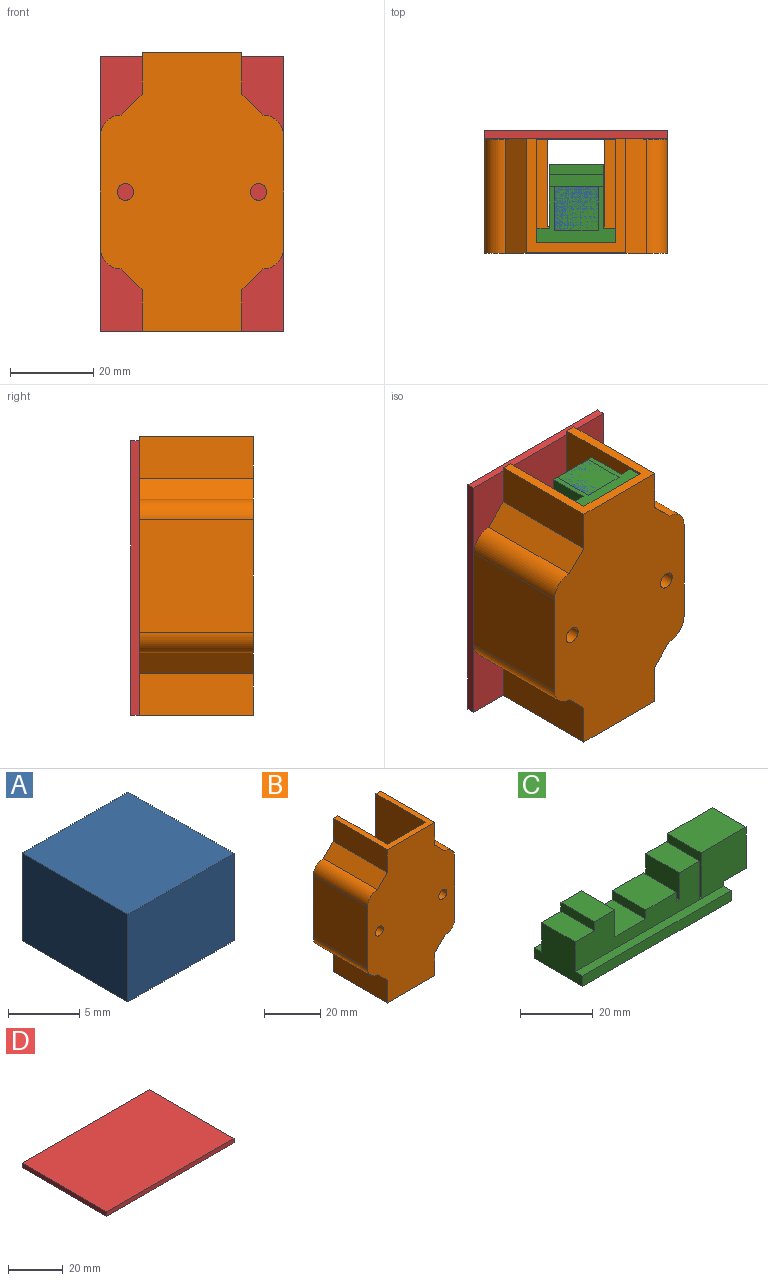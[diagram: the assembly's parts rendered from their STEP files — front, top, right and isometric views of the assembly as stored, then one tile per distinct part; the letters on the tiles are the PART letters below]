
ASSEMBLY  parts=4 mates=6
PART A: 10 faces, bbox 10.5x10.5x7.5 mm
  f0: plane 3.5x3.5mm, normal (0,1,0), area 9.6mm2, adj f2
  f1: plane 10.5x7.5mm, normal (0,-1,0), area 78.7mm2, adj f3,f4,f5,f6
  f2: cylinder r=1.75mm len=3.5mm, axis (0,-1,0), area 22mm2, adj f0,f7
  f3: plane 10.5x10.5mm, normal (0,0,-1), area 110.3mm2, adj f1,f4,f6,f7
  f4: plane 10.5x7.5mm, normal (-1,0,0), area 78.7mm2, adj f1,f3,f5,f7
  f5: plane 10.5x10.5mm, normal (0,0,1), area 110.3mm2, adj f1,f4,f6,f7
  f6: plane 10.5x7.5mm, normal (1,0,0), area 78.7mm2, adj f1,f3,f5,f7
  f7: plane 10.5x7.5mm, normal (0,1,0), area 59.5mm2, adj f2,f3,f4,f5,f6,f9
  f8: plane 3.5x3.5mm, normal (0,1,0), area 9.6mm2, adj f9
  f9: cylinder r=1.75mm len=3.5mm, axis (0,-1,0), area 22mm2, adj f7,f8
PART B: 34 faces, bbox 44x27.4x67 mm
  f0: plane 27.4x10mm, normal (-1,0,0), area 274mm2, adj f5,f11,f15,f23
  f1: plane 27.4x10mm, normal (1,0,0), area 274mm2, adj f5,f9,f14,f25
  f2: plane 60x19.2mm, normal (0,1,0), area 1152mm2, adj f8,f9,f10,f12
  f3: plane 21x7mm, normal (-1,0,0), area 147mm2, adj f11,f12,f13,f14
  f4: plane 27.4x10mm, normal (1,0,0), area 274mm2, adj f5,f11,f14,f22
  f5: plane 67x44mm, normal (0,-1,0), area 2351.4mm2, adj f0,f1,f4,f6,f9,f11,f16,f17
  f6: plane 27.4x10mm, normal (-1,0,0), area 274mm2, adj f5,f9,f15,f24
  f7: plane 21x7mm, normal (1,0,0), area 147mm2, adj f11,f12,f13,f15
  f8: plane 60x25mm, normal (1,0,0), area 1500mm2, adj f2,f9,f12,f15
  f9: plane 27.4x24mm, normal (0,0,1), area 177.6mm2, adj f1,f2,f5,f6,f8,f10,f14,f15
  f10: plane 60x25mm, normal (-1,0,0), area 1500mm2, adj f2,f9,f12,f14
  f11: plane 27.4x24mm, normal (0,0,-1), area 374.1mm2, adj f0,f3,f4,f5,f7,f13,f14,f15
  f12: plane 25x19.2mm, normal (0,0,1), area 196.5mm2, adj f2,f3,f7,f8,f10,f13,f14,f15
  f13: plane 13.5x7mm, normal (0,1,0), area 94.5mm2, adj f3,f7,f11,f12
  f14: plane 67x15.25mm, normal (0,1,0), area 512.7mm2, adj f1,f3,f4,f9,f10,f11,f12,f16
  f15: plane 67x15.25mm, normal (0,1,0), area 512.7mm2, adj f0,f6,f7,f8,f9,f11,f12,f17
  f16: plane 27.4x27mm, normal (1,0,0), area 739.8mm2, adj f5,f14,f20,f21
  f17: plane 27.4x27mm, normal (-1,0,0), area 739.8mm2, adj f5,f15,f18,f19
  f18: cylinder r=5mm len=27.4mm, axis (0,-1,0), area 215.2mm2, adj f5,f15,f17,f23
  f19: cylinder r=5mm len=27.4mm, axis (0,1,0), area 215.2mm2, adj f5,f15,f17,f24
  f20: cylinder r=5mm len=27.4mm, axis (0,1,0), area 215.2mm2, adj f5,f14,f16,f25
  f21: cylinder r=5mm len=27.4mm, axis (0,-1,0), area 215.2mm2, adj f5,f14,f16,f22
  f22: plane 27.4x5mm, normal (0.71,0,-0.71), area 193.7mm2, adj f4,f5,f14,f21
  f23: plane 27.4x5mm, normal (-0.71,0,-0.71), area 193.7mm2, adj f0,f5,f15,f18
  f24: plane 27.4x5mm, normal (-0.71,0,0.71), area 193.7mm2, adj f5,f6,f15,f19
  f25: plane 27.4x5mm, normal (0.71,0,0.71), area 193.7mm2, adj f1,f5,f14,f20
  f26: cylinder r=2mm len=25.9mm, axis (0,1,0), area 325.5mm2, adj f5,f27
  f27: cone r=2mm half-angle=45deg, axis (0,1,0), area 36.7mm2, adj f15,f26
  f28: cylinder r=2mm len=25.9mm, axis (0,1,0), area 325.5mm2, adj f5,f29
  f29: cone r=2mm half-angle=45deg, axis (0,1,0), area 36.7mm2, adj f14,f28
  f30: cone r=0mm half-angle=59deg, axis (0,1,0), area 16.2mm2, adj f31
  f31: cylinder r=2.1mm len=12mm, axis (0,1,0), area 158.3mm2, adj f15,f30
  f32: cone r=0mm half-angle=59deg, axis (0,1,0), area 16.2mm2, adj f33
  f33: cylinder r=2.1mm len=12mm, axis (0,1,0), area 158.3mm2, adj f14,f32
PART C: 26 faces, bbox 66.5x19x19 mm
  f0: plane 17.5x13mm, normal (0,0,1), area 227.5mm2, adj f8,f19,f23,f25
  f1: plane 57.7x3.5mm, normal (0,1,0), area 201.9mm2, adj f5,f20,f21,f24
  f2: plane 13x8mm, normal (0,0,1), area 104mm2, adj f9,f10,f23,f25
  f3: plane 13x12mm, normal (0,0,1), area 156mm2, adj f12,f13,f23,f25
  f4: plane 13x8mm, normal (0,0,1), area 104mm2, adj f15,f16,f23,f25
  f5: plane 19x13.5mm, normal (-1,0,0), area 196.5mm2, adj f1,f7,f18,f21,f22,f23,f24,f25
  f6: plane 13x8.8mm, normal (0,0,-1), area 114.4mm2, adj f19,f20,f23,f25
  f7: plane 13x7.5mm, normal (0,0,1), area 97.5mm2, adj f5,f9,f23,f25
  f8: plane 15x13mm, normal (-1,0,0), area 195mm2, adj f0,f17,f23,f25
  f9: plane 13x3mm, normal (-1,0,0), area 39mm2, adj f2,f7,f23,f25
  f10: plane 13x9mm, normal (1,0,0), area 117mm2, adj f2,f11,f23,f25
  f11: plane 13x12mm, normal (0,0,1), area 156mm2, adj f10,f12,f23,f25
  f12: plane 13x3mm, normal (-1,0,0), area 39mm2, adj f3,f11,f23,f25
  f13: plane 13x3mm, normal (1,0,0), area 39mm2, adj f3,f14,f23,f25
  f14: plane 13x1mm, normal (0,0,1), area 13mm2, adj f13,f15,f23,f25
  f15: plane 13x9mm, normal (-1,0,0), area 117mm2, adj f4,f14,f23,f25
  f16: plane 13x12.5mm, normal (1,0,0), area 162.5mm2, adj f4,f17,f23,f25
  f17: plane 13x0.5mm, normal (0,0,1), area 6.5mm2, adj f8,f16,f23,f25
  f18: plane 57.7x3.5mm, normal (0,-1,0), area 201.9mm2, adj f5,f20,f21,f22
  f19: plane 14x13mm, normal (1,0,0), area 182mm2, adj f0,f6,f23,f25
  f20: plane 19x5mm, normal (1,0,0), area 86mm2, adj f1,f6,f18,f21,f22,f23,f24,f25
  f21: plane 57.7x19mm, normal (0,0,-1), area 1096.3mm2, adj f1,f5,f18,f20
  f22: plane 57.7x3mm, normal (0,0,1), area 173.1mm2, adj f5,f18,f20,f23
  f23: plane 66.5x15.5mm, normal (0,-1,0), area 677.3mm2, adj f0,f2,f3,f4,f5,f6,f7,f8
  f24: plane 57.7x3mm, normal (0,0,1), area 173.1mm2, adj f1,f5,f20,f25
  f25: plane 66.5x15.5mm, normal (0,1,0), area 677.3mm2, adj f0,f2,f3,f4,f5,f6,f7,f8
PART D: 6 faces, bbox 66x44x2 mm
  f0: plane 44x2mm, normal (-1,0,0), area 88mm2, adj f1,f3,f4,f5
  f1: plane 66x2mm, normal (0,-1,0), area 132mm2, adj f0,f2,f4,f5
  f2: plane 44x2mm, normal (1,0,0), area 88mm2, adj f1,f3,f4,f5
  f3: plane 66x2mm, normal (0,1,0), area 132mm2, adj f0,f2,f4,f5
  f4: plane 66x44mm, normal (0,0,1), area 2904mm2, adj f0,f1,f2,f3
  f5: plane 66x44mm, normal (0,0,-1), area 2904mm2, adj f0,f1,f2,f3
PLACE A t=(3.39,-1.08,33.5)mm
PLACE B t=(3.29,-4.08,4.25)mm fixed
PLACE C rot(axis=(-0.58,0.58,0.58),120deg) t=(3.39,-4.08,8.15)mm
PLACE D rot(axis=(-0.58,-0.58,-0.58),120deg) t=(3.29,20.92,3.75)mm
MATE planar C.f18 <-> B.f10  axis (1,0,0) through (12.89,-2.33,8.4)mm
MATE planar D.f0 <-> B.f11  axis (0,0,-1) through (3.29,21.92,-29.25)mm
MATE planar B.f16 <-> D.f3  axis (1,0,0) through (25.29,7.22,4.25)mm
MATE planar D.f5 <-> B.f21  axis (0,-1,0) through (3.29,20.92,3.75)mm
MATE planar C.f21 <-> B.f2  axis (0,-1,0) through (3.39,-4.08,8.4)mm
MATE fastened A.f5 <-> C.f5  axis (0,0,1) through (3.39,9.42,37.25)mm
